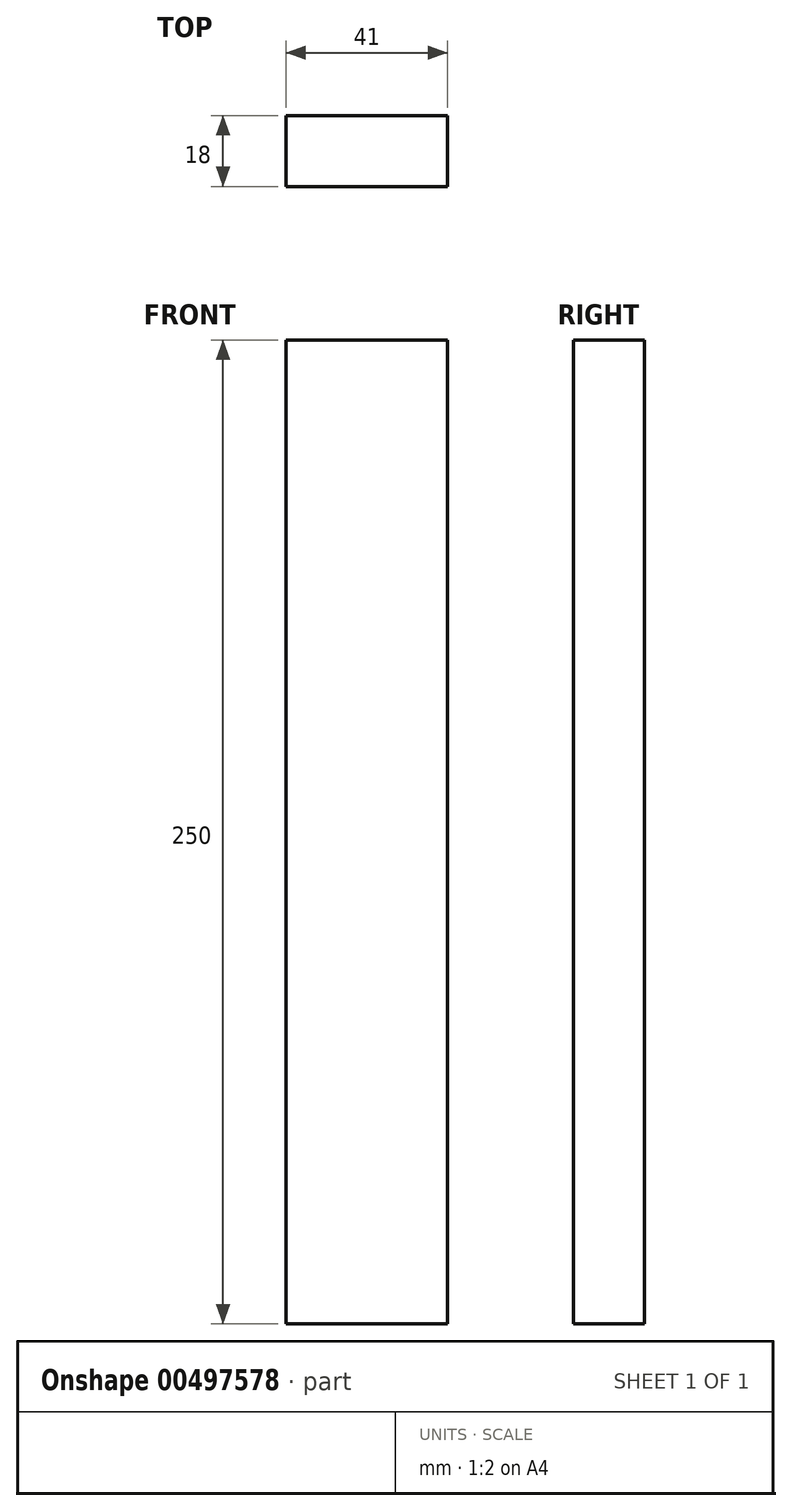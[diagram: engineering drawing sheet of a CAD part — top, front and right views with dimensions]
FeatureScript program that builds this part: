
annotation { "Feature Type Name" : "Feature", "Feature Type Description" : "" }
export const myFeature = defineFeature(function(context is Context, id is Id, definition is map)
    precondition{}
    {
        {
            var Q0;
            Q0=qCreatedBy(makeId("Front.planeOp"),FACE);
            var sketch = newSketch(context, id + "F0", { "sketchPlane" : qUnion([Q0])});
            skLineSegment(sketch, "E0.bottom", {"start": v(0, 0) * mm, "end": v(41, 0) * mm});
            skLineSegment(sketch, "E0.top", {"start": v(0, 250) * mm, "end": v(41, 250) * mm});
            skLineSegment(sketch, "E0.left", {"start": v(0, 0) * mm, "end": v(0, 250) * mm});
            skLineSegment(sketch, "E0.right", {"start": v(41, 0) * mm, "end": v(41, 250) * mm});
            skLineSegment(sketch, "E1", {"start": v(20.5, 250) * mm, "end": v(20.5, 0) * mm, "construction": true});
            skSolve(sketch);
        }
        {
            var Q0;
            Q0 = qSketchRegion(id + "F0", true);
            extrude(context, id + "F1", {"entities" : qUnion([Q0]), "depth" : 18 * mm, "offsetDistance" : 25.4 * mm});
        }
    });
